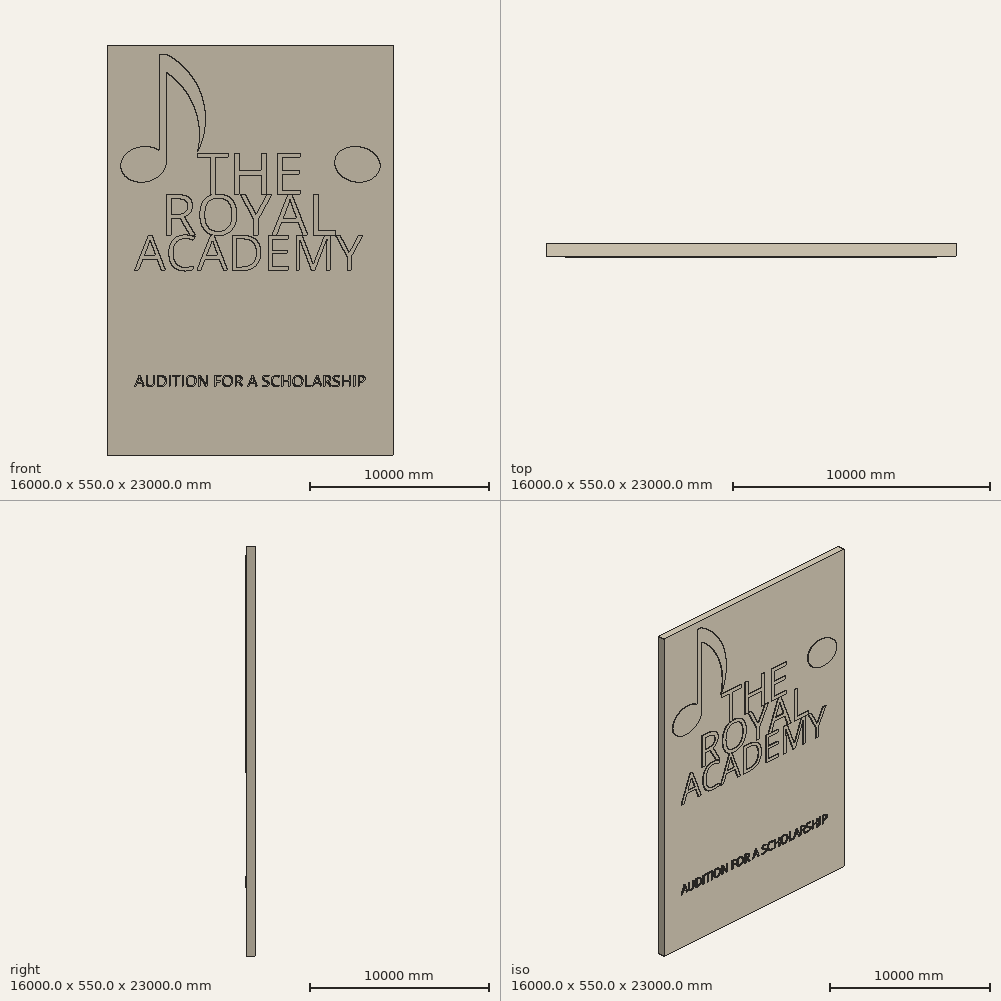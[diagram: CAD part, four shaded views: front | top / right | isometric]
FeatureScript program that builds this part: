
annotation { "Feature Type Name" : "Feature", "Feature Type Description" : "" }
export const myFeature = defineFeature(function(context is Context, id is Id, definition is map)
    precondition{}
    {
        {
            var Q0;
            Q0=qCreatedBy(makeId("Front.planeOp"),FACE);
            var sketch = newSketch(context, id + "F0", { "sketchPlane" : qUnion([Q0])});
            skLineSegment(sketch, "E0.bottom", {"start": v(-5020.46, 6023.68) * mm, "end": v(2979.54, 6023.68) * mm});
            skLineSegment(sketch, "E0.top", {"start": v(-5020.46, -5476.32) * mm, "end": v(2979.54, -5476.32) * mm});
            skLineSegment(sketch, "E0.left", {"start": v(-5020.46, 6023.68) * mm, "end": v(-5020.46, -5476.32) * mm});
            skLineSegment(sketch, "E0.right", {"start": v(2979.54, 6023.68) * mm, "end": v(2979.54, -5476.32) * mm});
            skSolve(sketch);
        }
        {
            var Q0;
            Q0=makeQuery(id+"F0.imprint","IMPRINT",FACE,{"disambiguationData":[TD([[makeQuery(id+"F0.imprint","IMPRINT",EDGE,{"derivedFrom":sQuery(id+"F0.wireOp",EDGE,"E0.bottom")}),-1.0]])]});
            extrude(context, id + "F1", {"entities" : qUnion([Q0]), "depth" : 500 * mm, "offsetDistance" : 25 * mm});
        }
        {
            var Q0;
            Q0=makeQuery(id+"F1.opExtrude","CAP_FACE",FACE,{"disambiguationData":[OSD([sQuery(id+"F0.wireOp",EDGE,"E0.bottom"),sQuery(id+"F0.wireOp",EDGE,"E0.top"),sQuery(id+"F0.wireOp",EDGE,"E0.left"),sQuery(id+"F0.wireOp",EDGE,"E0.right")])],"isStart":false});
            var sketch = newSketch(context, id + "F2", { "sketchPlane" : qUnion([Q0])});
            skLineSegment(sketch, "E1", {"start": v(-1020.46, 6023.68) * mm, "end": v(-5020.46, 6023.68) * mm});
            skLineSegment(sketch, "E2", {"start": v(-5020.46, 6023.68) * mm, "end": v(-5020.46, 273.68) * mm});
            skLineSegment(sketch, "E3", {"start": v(-5020.46, 273.68) * mm, "end": v(-5020.46, 3148.68) * mm});
            skLineSegment(sketch, "E4", {"start": v(-3020.46, 6023.68) * mm, "end": v(-3020.46, -645.56) * mm});
            skEllipse(sketch, "E5", {"center": v(-3020.46, -645.56) * mm, "majorRadius": 1283.25 * mm, "minorRadius": 993.76 * mm, "majorAxis": v(0.98, 0.18)});
            skLineSegment(sketch, "E6", {"start": v(-1758.12, -645.56) * mm, "end": v(-1758.12, 4530.6) * mm});
            skPoint(sketch, "E6.startSnap0", {"position": v(-1758.12, -414.8) * mm});
            skPoint(sketch, "E6.endSnap0", {"position": v(-1758.12, -414.8) * mm});
            skLineSegment(sketch, "E7", {"start": v(-1758.12, 4530.6) * mm, "end": v(-2108.12, 4530.6) * mm});
            skLineSegment(sketch, "E8", {"start": v(-2108.12, 4530.6) * mm, "end": v(-2108.12, 118.57) * mm});
            skArc(sketch, "E9", {"start": v(0, 0) * mm, "mid": v(-167.61, 2541.38) * mm, "end": v(-1758.12, 4530.6) * mm});
            skArc(sketch, "E10", {"start": v(0, 0) * mm, "mid": v(267.25, 3135.83) * mm, "end": v(-1758.12, 5544.7) * mm});
            skLineSegment(sketch, "E11", {"start": v(-2108.12, 4530.6) * mm, "end": v(-2108.12, 5544.7) * mm});
            skLineSegment(sketch, "E12", {"start": v(-2108.12, 5544.7) * mm, "end": v(-1758.12, 5544.7) * mm});
            skArc(sketch, "E13.MirrorCS", {"start": v(5959.08, 0) * mm, "mid": v(5691.84, 3135.83) * mm, "end": v(7717.2, 5544.7) * mm});
            skArc(sketch, "E14.MirrorCS", {"start": v(5959.08, 0) * mm, "mid": v(6126.7, 2541.38) * mm, "end": v(7717.2, 4530.6) * mm});
            skLineSegment(sketch, "E15.MirrorCS", {"start": v(7717.2, -645.56) * mm, "end": v(7717.2, 4530.6) * mm});
            skLineSegment(sketch, "E16.MirrorCS", {"start": v(8067.2, 4530.6) * mm, "end": v(8067.2, 118.57) * mm});
            skEllipse(sketch, "E17.MirrorC", {"center": v(8979.54, -645.56) * mm, "majorRadius": 1283.25 * mm, "minorRadius": 993.76 * mm, "majorAxis": v(-0.98, 0.18)});
            skLineSegment(sketch, "E18.MirrorCS", {"start": v(8067.2, 4530.6) * mm, "end": v(8067.2, 5544.7) * mm});
            skLineSegment(sketch, "E19.MirrorCS", {"start": v(8067.2, 5544.7) * mm, "end": v(7717.2, 5544.7) * mm});
            skLineSegment(sketch, "E20", {"start": v(0, 0) * mm, "end": v(5959.08, 0) * mm});
            skSolve(sketch);
        }
        {
            var Q0;
            {var subQ0=sQuery(id+"F2.wireOp",EDGE,"E5");var subQ1=makeQuery(id+"F2.imprint","INTERSECT",VERTEX,{"derivedFrom":[subQ0,sQuery(id+"F2.wireOp",EDGE,"E8")]});Q0=makeQuery(id+"F2.imprint","IMPRINT",FACE,{"disambiguationData":[TD([[makeQuery(id+"F2.imprint","IMPRINT",EDGE,{"disambiguationData":[TD([[subQ1,1.0]])],"derivedFrom":subQ0}),1.0]])]});}
            var Q1;
            {var subQ4=sQuery(id+"F2.wireOp",EDGE,"E7");Q1=makeQuery(id+"F2.imprint","IMPRINT",FACE,{"disambiguationData":[TD([[makeQuery(id+"F2.imprint","IMPRINT",EDGE,{"derivedFrom":subQ4}),1.0]])]});}
            var Q2;
            Q2=makeQuery(id+"F2.imprint","IMPRINT",FACE,{"disambiguationData":[TD([[makeQuery(id+"F2.imprint","IMPRINT",EDGE,{"derivedFrom":sQuery(id+"F2.wireOp",EDGE,"E7")}),-1.0]])]});
            extrude(context, id + "F3", {"entities" : qUnion([Q0, Q1, Q2]), "depth" : 50 * mm, "offsetDistance" : 25 * mm});
        }
        {
            var Q0;
            Q0=makeQuery(id+"F1.opExtrude","SWEPT_FACE",FACE,{"disambiguationData":[OSD([sQuery(id+"F0.wireOp",EDGE,"E0.right")])]});
            extrude(context, id + "F4", {"entities" : qUnion([Q0]), "operationType" : NewBodyOperationType.ADD, "depth" : 8000 * mm, "offsetDistance" : 25 * mm});
        }
        {
            var Q0;
            {var subQ0=sQuery(id+"F0.wireOp",EDGE,"E0.top");Q0=makeQuery(id+"F4.boolean.opBoolean","MERGE",FACE,{"derivedFrom":[makeQuery(id+"F1.opExtrude","SWEPT_FACE",FACE,{"disambiguationData":[OSD([subQ0])]}),makeQuery(id+"F4.opExtrude","SWEPT_FACE",FACE,{"disambiguationData":[OSD([subQ0,sQuery(id+"F0.wireOp",EDGE,"E0.right")])]})]});}
            extrude(context, id + "F5", {"entities" : qUnion([Q0]), "operationType" : NewBodyOperationType.ADD, "depth" : 11500 * mm, "offsetDistance" : 25 * mm});
        }
        {
            var Q0;
            Q0=makeQuery(id+"F2.imprint","IMPRINT",FACE,{"disambiguationData":[TD([[makeQuery(id+"F2.imprint","IMPRINT",EDGE,{"derivedFrom":sQuery(id+"F2.wireOp",EDGE,"E13.MirrorCS")}),-1.0]])]});
            var Q1;
            {var subQ0=sQuery(id+"F2.wireOp",EDGE,"E17.MirrorC");var subQ1=makeQuery(id+"F2.imprint","INTERSECT",VERTEX,{"derivedFrom":[sQuery(id+"F2.wireOp",EDGE,"E16.MirrorCS"),subQ0]});Q1=makeQuery(id+"F2.imprint","IMPRINT",FACE,{"disambiguationData":[TD([[makeQuery(id+"F2.imprint","IMPRINT",EDGE,{"disambiguationData":[TD([[subQ1,1.0]])],"derivedFrom":subQ0}),1.0]])]});}
            extrude(context, id + "F6", {"entities" : qUnion([Q0, Q1]), "operationType" : NewBodyOperationType.ADD, "depth" : 50 * mm, "offsetDistance" : 25 * mm});
        }
        {
            var Q0;
            {var subQ0=sQuery(id+"F0.wireOp",EDGE,"E0.right");var subQ1=sQuery(id+"F0.wireOp",EDGE,"E0.top");Q0=makeQuery(id+"F5.boolean.opBoolean","MERGE",FACE,{"derivedFrom":[makeQuery(id+"F4.boolean.opBoolean","MERGE",FACE,{"derivedFrom":[makeQuery(id+"F1.opExtrude","CAP_FACE",FACE,{"disambiguationData":[OSD([sQuery(id+"F0.wireOp",EDGE,"E0.bottom"),subQ1,sQuery(id+"F0.wireOp",EDGE,"E0.left"),subQ0])],"isStart":false}),makeQuery(id+"F4.opExtrude","SWEPT_FACE",FACE,{"disambiguationData":[OSD([subQ0]),TDD([makeQuery(id+"F1.opExtrude","CAP_EDGE",EDGE,{"disambiguationData":[OSD([subQ0])],"isStart":false})])]})]}),makeQuery(id+"F5.opExtrude","SWEPT_FACE",FACE,{"disambiguationData":[OSD([subQ1,subQ0]),TDD([makeQuery(id+"F4.boolean.opBoolean","MERGE",EDGE,{"derivedFrom":[makeQuery(id+"F1.opExtrude","CAP_EDGE",EDGE,{"disambiguationData":[OSD([subQ1])],"isStart":false}),makeQuery(id+"F4.opExtrude","SWEPT_EDGE",EDGE,{"disambiguationData":[OSD([subQ1,subQ0]),TDD([makeQuery(id+"F1.opExtrude","CAP_VERTEX",VERTEX,{"disambiguationData":[OSD([subQ1,subQ0])],"isStart":false})])]})]})])]})]});}
            var sketch = newSketch(context, id + "F7", { "sketchPlane" : qUnion([Q0])});
            skText(sketch, "E21", { "text": "THE", "fontName": "OpenSans-Regular.ttf"});
            skLineSegment(sketch, "E22", {"start": v(0, 0) * mm, "end": v(5959.08, 0) * mm});
            skLineSegment(sketch, "E23", {"start": v(2979.54, 6023.68) * mm, "end": v(-5020.46, 6023.68) * mm});
            skLineSegment(sketch, "E24", {"start": v(2979.54, 6023.68) * mm, "end": v(10979.54, 6023.68) * mm});
            skLineSegment(sketch, "E25", {"start": v(-5020.46, 6023.68) * mm, "end": v(-1020.46, 6023.68) * mm});
            skLineSegment(sketch, "E26", {"start": v(-1020.46, 6023.68) * mm, "end": v(-3020.46, 6023.68) * mm});
            skLineSegment(sketch, "E27", {"start": v(6979.54, 6023.68) * mm, "end": v(10979.54, 6023.68) * mm});
            skLineSegment(sketch, "E28", {"start": v(8979.54, 6023.68) * mm, "end": v(6979.54, 6023.68) * mm});
            skText(sketch, "E29", { "text": "ROYAL", "fontName": "OpenSans-Regular.ttf"});
            skPoint(sketch, "E29.firstSnap0", {"position": v(-2020.46, 6023.68) * mm});
            skPoint(sketch, "E29.secondSnap0", {"position": v(7979.54, 6023.68) * mm});
            skLineSegment(sketch, "E30", {"start": v(-2020.46, 6023.68) * mm, "end": v(-2020.46, -12487.92) * mm});
            skLineSegment(sketch, "E31", {"start": v(-2020.46, -4613.81) * mm, "end": v(-5020.46, -4613.81) * mm});
            skLineSegment(sketch, "E32", {"start": v(7979.54, -4613.81) * mm, "end": v(10979.54, -4613.81) * mm});
            skText(sketch, "E33", { "text": "ACADEMY", "fontName": "OpenSans-Regular.ttf"});
            skPoint(sketch, "E33.secondSnap0", {"position": v(9479.54, -4613.81) * mm});
            skText(sketch, "E34", { "text": "AUDITION FOR A SCHOLARSHIP", "fontName": "OpenSans-Regular.ttf"});
            const initialGuessF7  = {"E21": [0, -2.32855, 1, 0, 2.32855], "E29": [-2.02046, -4.61381, 1, 0, 2.28526], "E33": [-3.52046, -6.60134, 1, 0, 1.98752], "E34": [-3.52046, -13.12439, 1, 0, 0.63647]};
            skSetInitialGuess(sketch, initialGuessF7);
            skSolve(sketch);
        }
        {
            var Q0;
            Q0 = qSketchRegion(id + "F7", true);
            extrude(context, id + "F8", {"entities" : qUnion([Q0]), "depth" : 50 * mm, "offsetDistance" : 25 * mm});
        }
    });
